# Revit family: ULS –profiili
name_source: partatom
category: Windows
revit_build: Autodesk Revit Architecture 2014 (Build: 20130709_2115(x64)
units: mm (PartAtom-declared; Revit-internal decimal feet)

## types (13) — shared parameters
Analytic Construction = <None>
Description = -
Frame Material = Metalli - alumiini, satiini
Frame Thickness = 50 mm  [stored 0.164042 ft]
Glass Material = Lasi - 1 lasilevy, kirkas
Keynote = 1349
Manufacturer = -
Model = -
Sash Material = Metalli - alumiini, satiini
Transom Placement = 900 mm  [stored 2.95276 ft]
Wall Closure = By host
zero-valued in all types: Cost, Cost VAT_0, Default Sill Height

## per-type parameters (varying)
| type | Frame Depth | Height | Height_M | ID | Width | Width_M |
| 12x21 | 100 mm  [stored 0.328084 ft] | 2400 mm | 24 mm  [stored 0.0787402 ft] | IKK11 | 1000 mm  [stored 3.28084 ft] | 10 mm  [stored 0.0328084 ft] |
| 3x24 | 100 mm  [stored 0.328084 ft] | 2400 mm | 24 mm  [stored 0.0787402 ft] | IKK11 | 300 mm | 3 mm  [stored 0.00984252 ft] |
| 5x24 | 100 mm  [stored 0.328084 ft] | 2400 mm | 24 mm  [stored 0.0787402 ft] | IKK11 | 500 mm  [stored 1.64042 ft] | 5 mm  [stored 0.0164042 ft] |
| 7x24 | 100 mm  [stored 0.328084 ft] | 2400 mm | 24 mm  [stored 0.0787402 ft] | IKK11 | 700 mm  [stored 2.29659 ft] | 7 mm  [stored 0.0229659 ft] |
| 10x24 | 100 mm  [stored 0.328084 ft] | 2400 mm | 24 mm  [stored 0.0787402 ft] | IKK11 | 1000 mm  [stored 3.28084 ft] | 10 mm  [stored 0.0328084 ft] |
| 12x24 | 100 mm  [stored 0.328084 ft] | 2400 mm | 24 mm  [stored 0.0787402 ft] | IKK11 | 1200 mm | 12 mm  [stored 0.0393701 ft] |
| ULS 43 | 210 mm  [stored 0.688976 ft] | 10400 mm  [stored 34.1207 ft] | 104 mm |  | 4300 mm | 43 mm  [stored 0.141076 ft] |
| ULS 45.5 3KRS | 210 mm  [stored 0.688976 ft] | 3600 mm  [stored 11.811 ft] | 36 mm  [stored 0.11811 ft] |  | 4550 mm | 46 mm |
| ULS 42.5 | 210 mm  [stored 0.688976 ft] | 6800 mm  [stored 22.3097 ft] | 68 mm |  | 4250 mm | 43 mm  [stored 0.141076 ft] |
| ULS 45.5 | 210 mm  [stored 0.688976 ft] | 10400 mm  [stored 34.1207 ft] | 104 mm |  | 4550 mm | 46 mm |
| ULS 43 3KRS | 210 mm  [stored 0.688976 ft] | 3600 mm  [stored 11.811 ft] | 36 mm  [stored 0.11811 ft] |  | 4300 mm | 43 mm  [stored 0.141076 ft] |
| ULS 53.5 | 210 mm  [stored 0.688976 ft] | 3200 mm  [stored 10.4987 ft] | 32 mm  [stored 0.104987 ft] |  | 5350 mm  [stored 17.5525 ft] | 54 mm |
| ULS 58 | 210 mm  [stored 0.688976 ft] | 3200 mm  [stored 10.4987 ft] | 32 mm  [stored 0.104987 ft] |  | 5800 mm  [stored 19.0289 ft] | 58 mm  [stored 0.190289 ft] |

note: [stored X ft] marks values corroborated as IEEE doubles in the binary element streams (Revit-internal decimal feet)

## geometry (parser evidence)
native form markers: Blend x4, Sweep x7
no freeform markers — native parametric forms only
